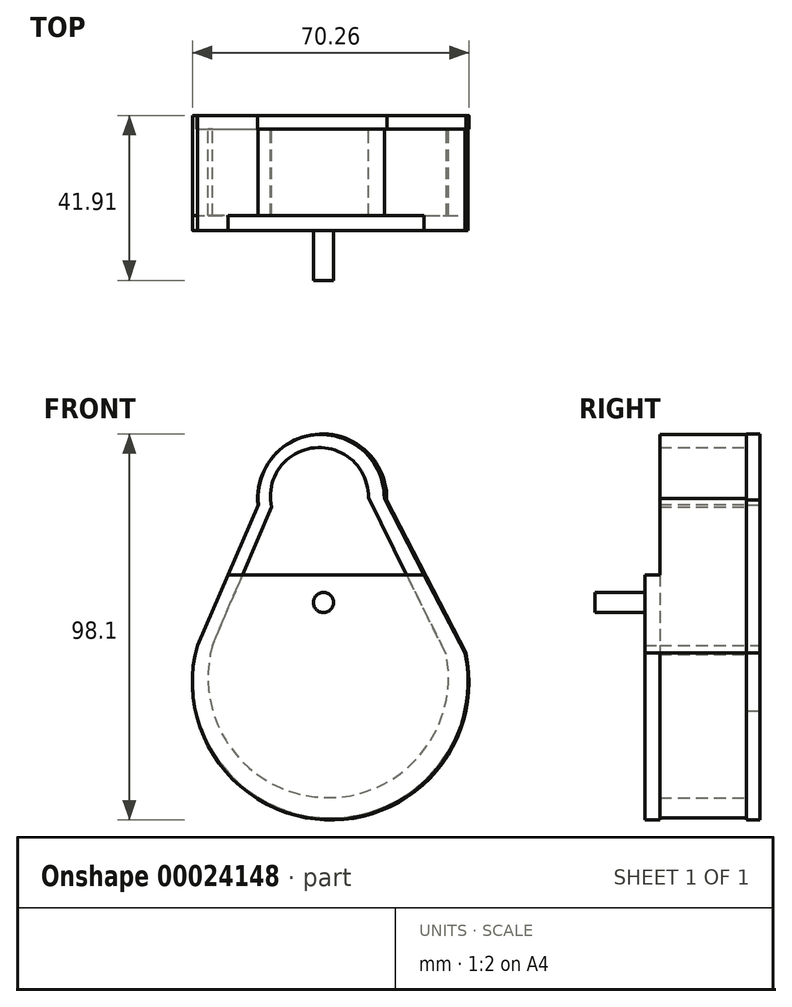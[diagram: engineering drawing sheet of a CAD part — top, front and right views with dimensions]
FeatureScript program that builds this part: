
annotation { "Feature Type Name" : "Feature", "Feature Type Description" : "" }
export const myFeature = defineFeature(function(context is Context, id is Id, definition is map)
    precondition{}
    {
        {
            var Q0;
            Q0=qCreatedBy(makeId("Front.planeOp"),FACE);
            var sketch = newSketch(context, id + "F0", { "sketchPlane" : qUnion([Q0])});
            skArc(sketch, "E0", {"start": v(17, 34.64) * mm, "mid": v(-0.41, 51.4) * mm, "end": v(-15.6, 32.6) * mm});
            skArc(sketch, "E1", {"start": v(-31.13, -3.1) * mm, "mid": v(2.25, -46.68) * mm, "end": v(37.09, -4.24) * mm});
            skLineSegment(sketch, "E2", {"start": v(-15.6, 32.6) * mm, "end": v(-31.13, -3.1) * mm});
            skLineSegment(sketch, "E3", {"start": v(17, 34.64) * mm, "end": v(37.09, -4.24) * mm});
            skSolve(sketch);
        }
        {
            var Q0;
            Q0=makeQuery(id+"F0.imprint","IMPRINT",FACE,{"disambiguationData":[TD([[makeQuery(id+"F0.imprint","IMPRINT",EDGE,{"derivedFrom":sQuery(id+"F0.wireOp",EDGE,"E0")}),1.0]])]});
            extrude(context, id + "F1", {"entities" : qUnion([Q0]), "depth" : 3.45 * mm});
        }
        {
            var Q0;
            Q0=qCreatedBy(makeId("Front.planeOp"),FACE);
            var sketch = newSketch(context, id + "F2", { "sketchPlane" : qUnion([Q0])});
            skArc(sketch, "E4", {"start": v(16.38, 34.96) * mm, "mid": v(-0.38, 51.24) * mm, "end": v(-15.6, 33.53) * mm});
            skArc(sketch, "E5", {"start": v(-31.13, -2.28) * mm, "mid": v(1.69, -46.17) * mm, "end": v(36.9, -4.19) * mm});
            skArc(sketch, "E6", {"start": v(12.32, 35.21) * mm, "mid": v(-1.33, 47.9) * mm, "end": v(-12.27, 32.81) * mm});
            skArc(sketch, "E7", {"start": v(-27.3, -2.28) * mm, "mid": v(0.9, -40.97) * mm, "end": v(32.13, -4.67) * mm});
            skLineSegment(sketch, "E8", {"start": v(12.32, 35.21) * mm, "end": v(32.13, -4.67) * mm});
            skLineSegment(sketch, "E9", {"start": v(-12.27, 32.81) * mm, "end": v(-27.3, -2.28) * mm});
            skLineSegment(sketch, "E10", {"start": v(-15.6, 33.53) * mm, "end": v(-31.13, -2.28) * mm});
            skLineSegment(sketch, "E11", {"start": v(16.38, 34.96) * mm, "end": v(36.9, -4.19) * mm});
            skSolve(sketch);
        }
        {
            var Q0;
            Q0 = qSketchRegion(id + "F2", true);
            extrude(context, id + "F3", {"entities" : qUnion([Q0]), "operationType" : NewBodyOperationType.ADD, "depth" : 25.4 * mm});
        }
        {
            var Q0;
            Q0=makeQuery(id+"F3.opExtrude","CAP_FACE",FACE,{"disambiguationData":[OSD([sQuery(id+"F2.wireOp",EDGE,"E4"),sQuery(id+"F2.wireOp",EDGE,"E5"),sQuery(id+"F2.wireOp",EDGE,"E6"),sQuery(id+"F2.wireOp",EDGE,"E7"),sQuery(id+"F2.wireOp",EDGE,"E8"),sQuery(id+"F2.wireOp",EDGE,"E9"),sQuery(id+"F2.wireOp",EDGE,"E10"),sQuery(id+"F2.wireOp",EDGE,"E11")])],"isStart":false});
            var sketch = newSketch(context, id + "F4", { "sketchPlane" : qUnion([Q0])});
            skArc(sketch, "E12", {"start": v(-31.13, -2.28) * mm, "mid": v(1.68, -46.58) * mm, "end": v(36.9, -4.19) * mm});
            skLineSegment(sketch, "E13", {"start": v(-31.13, -2.28) * mm, "end": v(-23.37, 15.62) * mm});
            skLineSegment(sketch, "E14", {"start": v(36.9, -4.19) * mm, "end": v(26.52, 15.62) * mm});
            skLineSegment(sketch, "E15", {"start": v(-23.37, 15.62) * mm, "end": v(26.52, 15.62) * mm});
            skSolve(sketch);
        }
        {
            var Q0;
            Q0 = qSketchRegion(id + "F4", true);
            extrude(context, id + "F5", {"entities" : qUnion([Q0]), "operationType" : NewBodyOperationType.ADD, "depth" : 3.8 * mm});
        }
        {
            var Q0;
            Q0=makeQuery(id+"F5.opExtrude","CAP_FACE",FACE,{"disambiguationData":[OSD([sQuery(id+"F4.wireOp",EDGE,"E12"),sQuery(id+"F4.wireOp",EDGE,"E13"),sQuery(id+"F4.wireOp",EDGE,"E14"),sQuery(id+"F4.wireOp",EDGE,"E15")])],"isStart":false});
            var sketch = newSketch(context, id + "F6", { "sketchPlane" : qUnion([Q0])});
            skCircle(sketch, "E16", {"center": v(0.92, 8.58) * mm, "radius": 2.56 * mm});
            skSolve(sketch);
        }
        {
            var Q0;
            Q0 = qSketchRegion(id + "F6", true);
            extrude(context, id + "F7", {"entities" : qUnion([Q0]), "operationType" : NewBodyOperationType.ADD, "depth" : 12.7 * mm});
        }
    });
